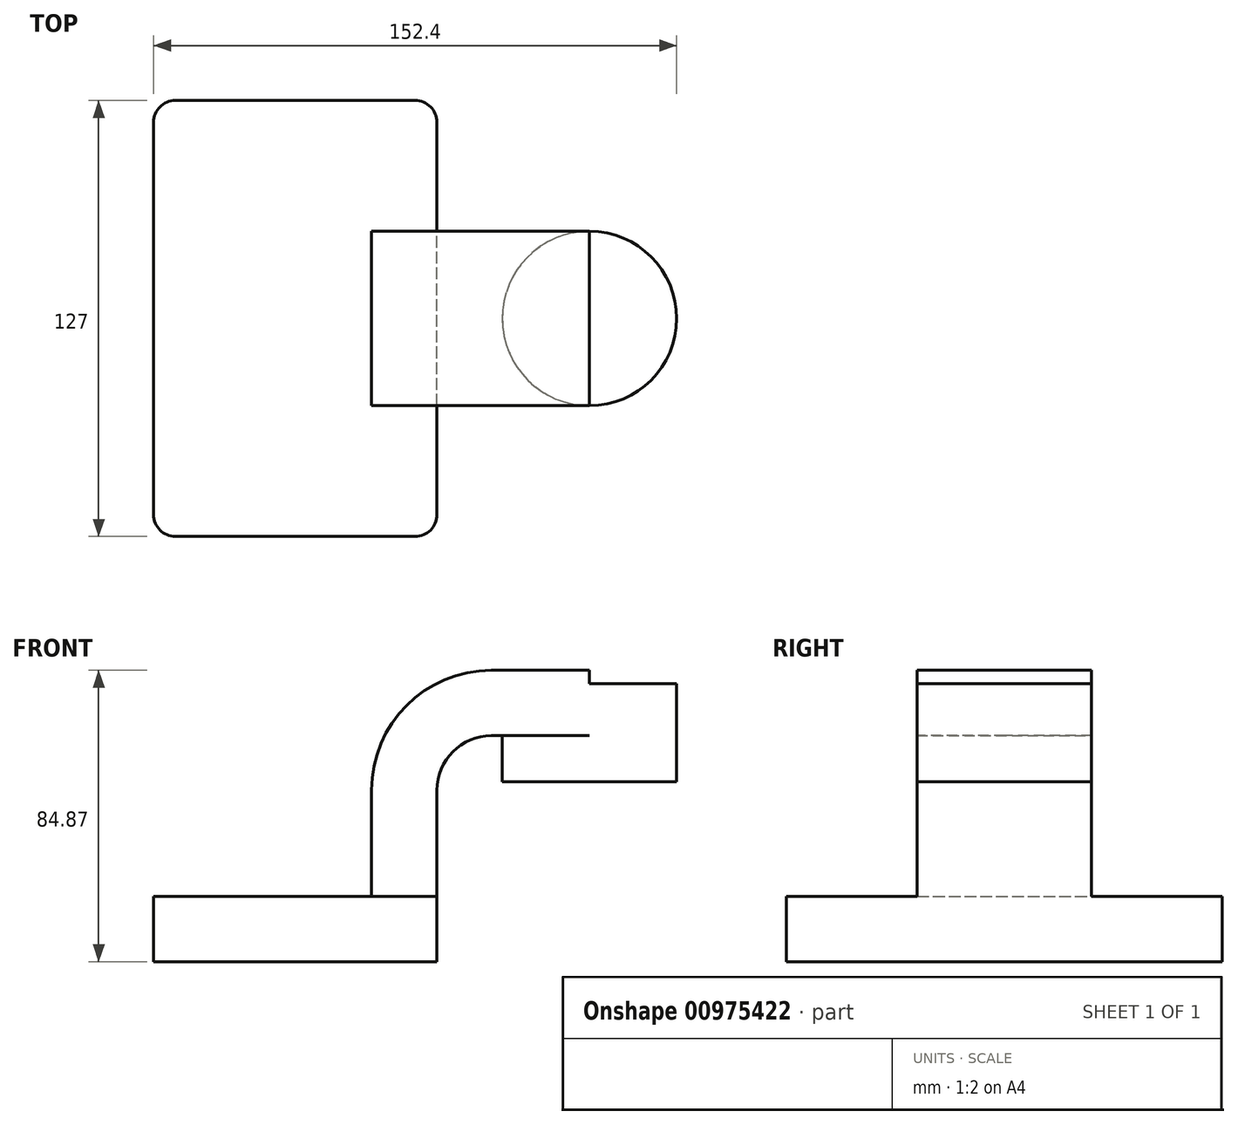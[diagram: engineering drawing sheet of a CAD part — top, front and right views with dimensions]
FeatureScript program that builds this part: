
annotation { "Feature Type Name" : "Feature", "Feature Type Description" : "" }
export const myFeature = defineFeature(function(context is Context, id is Id, definition is map)
    precondition{}
    {
        {
            var Q0;
            Q0=qCreatedBy(makeId("Front.planeOp"),FACE);
            var sketch = newSketch(context, id + "F0", { "sketchPlane" : qUnion([Q0])});
            skLineSegment(sketch, "E0.bottom", {"start": v(-41.28, -9.53) * mm, "end": v(41.28, -9.53) * mm});
            skLineSegment(sketch, "E0.top", {"start": v(-41.28, 9.53) * mm, "end": v(41.28, 9.53) * mm});
            skLineSegment(sketch, "E0.left", {"start": v(-41.28, -9.53) * mm, "end": v(-41.28, 9.53) * mm});
            skLineSegment(sketch, "E0.right", {"start": v(41.28, -9.53) * mm, "end": v(41.28, 9.53) * mm});
            skPoint(sketch, "E0.middle", {"position": v(0, 0) * mm});
            skLineSegment(sketch, "E1.bottom", {"start": v(60.33, 71.45) * mm, "end": v(111.13, 71.45) * mm});
            skLineSegment(sketch, "E1.top", {"start": v(60.33, 42.88) * mm, "end": v(111.13, 42.88) * mm});
            skLineSegment(sketch, "E1.left", {"start": v(60.33, 71.45) * mm, "end": v(60.32, 42.88) * mm});
            skLineSegment(sketch, "E1.right", {"start": v(111.13, 71.45) * mm, "end": v(111.13, 42.88) * mm});
            skPoint(sketch, "E1.middle", {"position": v(85.72, 57.16) * mm});
            skLineSegment(sketch, "E2", {"start": v(41.28, 9.53) * mm, "end": v(41.28, 40.41) * mm});
            skArc(sketch, "E3", {"start": v(41.28, 40.41) * mm, "mid": v(45.92, 51.64) * mm, "end": v(57.15, 56.29) * mm});
            skLineSegment(sketch, "E4", {"start": v(57.15, 56.29) * mm, "end": v(89.94, 56.29) * mm});
            skLineSegment(sketch, "E5.0", {"start": v(57.15, 75.34) * mm, "end": v(89.94, 75.34) * mm});
            skArc(sketch, "E5.1", {"start": v(22.23, 40.41) * mm, "mid": v(32.45, 65.1) * mm, "end": v(57.15, 75.34) * mm});
            skLineSegment(sketch, "E5.2", {"start": v(22.22, 9.53) * mm, "end": v(22.22, 40.41) * mm});
            skLineSegment(sketch, "E6", {"start": v(85.73, 42.88) * mm, "end": v(85.73, 75.34) * mm});
            skFitSpline(sketch, "E7", {"points": [v(-41.28, 9.53) * mm, v(57.15, 75.34) * mm], "startDerivative": vector(3.34, 76.48) * mm, "endDerivative": vector(111.74, -0.66) * mm});
            skSolve(sketch);
        }
        {
            var Q0;
            Q0=makeQuery(id+"F0.imprint","IMPRINT",FACE,{"disambiguationData":[TD([[makeQuery(id+"F0.imprint","IMPRINT",EDGE,{"derivedFrom":sQuery(id+"F0.wireOp",EDGE,"E0.bottom")}),1.0]])]});
            extrude(context, id + "F1", {"entities" : qUnion([Q0]), "endBound" : BoundingType.SYMMETRIC, "depth" : 127 * mm, "offsetDistance" : 25.4 * mm});
        }
        {
            var Q0;
            {var subQ10=sQuery(id+"F0.wireOp",EDGE,"E2");Q0=makeQuery(id+"F0.imprint","IMPRINT",FACE,{"disambiguationData":[TD([[makeQuery(id+"F0.imprint","IMPRINT",EDGE,{"derivedFrom":subQ10}),1.0]])]});}
            var Q1;
            {var subQ0=sQuery(id+"F0.wireOp",EDGE,"E1.left");var subQ1=sQuery(id+"F0.wireOp",EDGE,"E1.bottom");var subQ2=makeQuery(id+"F0.imprint","INTERSECT",VERTEX,{"derivedFrom":[subQ1,subQ0]});Q1=makeQuery(id+"F0.imprint","IMPRINT",FACE,{"disambiguationData":[TD([[makeQuery(id+"F0.imprint","IMPRINT",EDGE,{"disambiguationData":[TD([[subQ2,-1.0]])],"derivedFrom":subQ1}),-1.0]])]});}
            extrude(context, id + "F2", {"entities" : qUnion([Q0, Q1]), "operationType" : NewBodyOperationType.ADD, "endBound" : BoundingType.SYMMETRIC, "depth" : 50.8 * mm, "offsetDistance" : 25.4 * mm});
        }
        {
            var Q0;
            Q0=makeQuery(id+"F0.imprint","IMPRINT",FACE,{"disambiguationData":[TD([[makeQuery(id+"F0.imprint","IMPRINT",EDGE,{"derivedFrom":sQuery(id+"F0.wireOp",EDGE,"E5.1")}),1.0]])]});
            extrude(context, id + "F3", {"entities" : qUnion([Q0]), "operationType" : NewBodyOperationType.ADD, "endBound" : BoundingType.SYMMETRIC, "depth" : 15.88 * mm, "offsetDistance" : 25.4 * mm});
        }
        {
            var Q0;
            {var subQ4=sQuery(id+"F0.wireOp",EDGE,"E1.right");Q0=makeQuery(id+"F0.imprint","IMPRINT",FACE,{"disambiguationData":[TD([[makeQuery(id+"F0.imprint","IMPRINT",EDGE,{"derivedFrom":subQ4}),-1.0]])]});}
            var Q1;
            Q1=sQuery(id+"F0.wireOp",EDGE,"E6");
            revolve(context, id + "F4", {"operationType" : NewBodyOperationType.ADD, "surfaceOperationType" : NewSurfaceOperationType.NEW, "entities" : qUnion([Q0]), "axis" : qUnion([Q1]), "revolveType" : RevolveType.FULL});
        }
        {
            var Q0;
            Q0=makeQuery(id+"F1.opExtrude","CAP_EDGE",EDGE,{"disambiguationData":[OSD([sQuery(id+"F0.wireOp",EDGE,"E0.right")])],"isStart":false});
            var Q1;
            Q1=makeQuery(id+"F1.opExtrude","CAP_EDGE",EDGE,{"disambiguationData":[OSD([sQuery(id+"F0.wireOp",EDGE,"E0.left")])],"isStart":false});
            var Q2;
            Q2=makeQuery(id+"F1.opExtrude","CAP_EDGE",EDGE,{"disambiguationData":[OSD([sQuery(id+"F0.wireOp",EDGE,"E0.left")])],"isStart":true});
            var Q3;
            Q3=makeQuery(id+"F1.opExtrude","CAP_EDGE",EDGE,{"disambiguationData":[OSD([sQuery(id+"F0.wireOp",EDGE,"E0.right")])],"isStart":true});
            fillet(context, id + "F5", {"entities" : qUnion([Q0, Q1, Q2, Q3]), "radius" : 6.35 * mm, "tangentPropagation" : true, "allowEdgeOverflow" : false});
        }
    });
